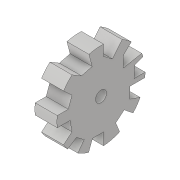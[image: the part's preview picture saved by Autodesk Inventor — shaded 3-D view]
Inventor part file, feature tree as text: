
AUTODESK INVENTOR PART (.ipt)
format: ipt  version: 2019 (Build 230136000, 136)  size: 156,672 bytes
history: native  units: in
note: dims shown in document units (in); Inventor stores cm internally (conversion verified against a paired STEP export)
features: extrude x4, sketch x4
ambient origin geometry x8: Origin, YZ Plane, XZ Plane, XY Plane, X Axis, Y Axis, Z Axis, Center Point
bodies: Solid1 (feature_tree)
feature tree (8):
  extrude  "Extrusion1"  Depth=0.7874in TaperAngle=0.0deg
  extrude  "Extrusion2"  Depth=0.3937in
  extrude  "Extrusion3"  Depth=0.3937in
  extrude  "Extrusion4"  Depth=0.3937in
  sketch  "Sketch1"  dims[d0=3.1496in d1=0.7874in d2=0.0in]
  sketch  "Sketch2"  dims[d3=0.3937in d4=0.3937in]
  sketch  "Sketch3"  dims[d5=0.3937in d6=0.3937in]
  sketch  "Sketch4"  dims[d7=0.3937in d8=0.3937in d9=0.3937in d10=0.3937in d11=0.3937in d12=0.3937in d13=0.3937in d14=0.3937in d15=0.3937in d16=0.3937in d17=0.3937in d18=0.7874in d19=0.0in d20=0.7874in d21=0.0in d22=0.3937in d23=0.7874in d24=0.0in]
